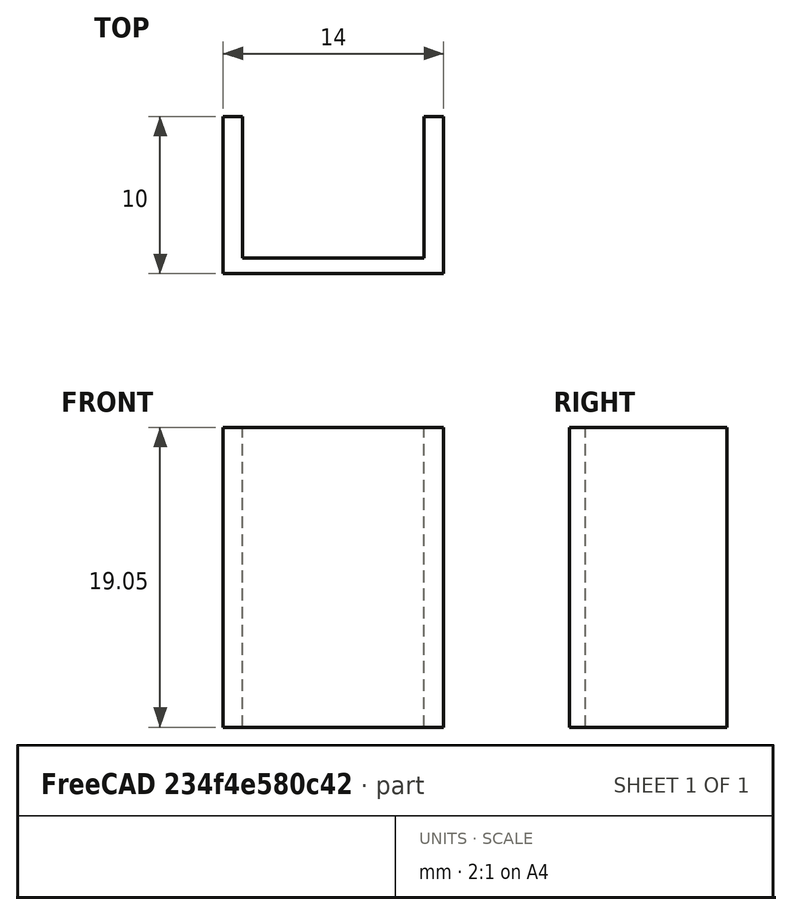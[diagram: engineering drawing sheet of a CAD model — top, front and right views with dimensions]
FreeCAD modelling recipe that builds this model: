
FCSTD DOCUMENT  (FreeCAD 0.19R)
Label: heatsink
License: All rights reserved
LicenseURL: http://en.wikipedia.org/wiki/All_rights_reserved
objects: Sketcher::SketchObject×1, PartDesign::Pad×1, PartDesign::Body×1
note: 4 computed .brp shape members not serialized (recipe doc carries the construction recipe); baked Part::Feature solids carry a one-line shape summary decoded from their .brp

FEATURE [Sketcher::SketchObject] Sketch
  FullyConstrained = false
  MapMode = 5
  Support = -> [XY_Plane]
  sketch-geometry (8):
    g0: LineSegment StartX=0 StartY=0 StartZ=0 EndX=14 EndY=0 EndZ=0
    g1: LineSegment StartX=14 StartY=0 StartZ=0 EndX=14 EndY=10 EndZ=0
    g2: LineSegment StartX=0 StartY=0 StartZ=0 EndX=0 EndY=10 EndZ=0
    g3: LineSegment StartX=0 StartY=10 StartZ=0 EndX=1.23616 EndY=10 EndZ=0
    g4: LineSegment StartX=14 StartY=10 StartZ=0 EndX=12.7619 EndY=10 EndZ=0
    g5: LineSegment StartX=1.23616 StartY=10 StartZ=0 EndX=1.23616 EndY=1 EndZ=0
    g6: LineSegment StartX=12.7619 StartY=10 StartZ=0 EndX=12.7619 EndY=1 EndZ=0
    g7: LineSegment StartX=1.23616 StartY=1 StartZ=0 EndX=12.7619 EndY=1 EndZ=0
  constraints (17):
    c: Coincident(g0,g-1)
    c: PointOnObject(g0,g-1)
    c: Coincident(g1,g0)
    c: Vertical(g1)
    c: Coincident(g2,g0)
    c: PointOnObject(g2,g-2)
    c: Coincident(g3,g2)
    c: Horizontal(g3)
    c: Coincident(g4,g1)
    c: Horizontal(g4)
    c: Coincident(g5,g3)
    c: Vertical(g5)
    c: Coincident(g6,g4)
    c: Vertical(g6)
    c: Coincident(g7,g5)
    c: Coincident(g7,g6)
    c: Horizontal(g7)
FEATURE [PartDesign::Pad] Pad
  Direction = (1,1,1)
  Length = 19.05
  Length2 = 100
  Profile = -> Sketch
  Type = 0
FEATURE [PartDesign::Body] Body
  Group = -> [Sketch,Pad]
  Origin = -> Origin
  Tip = -> Pad
